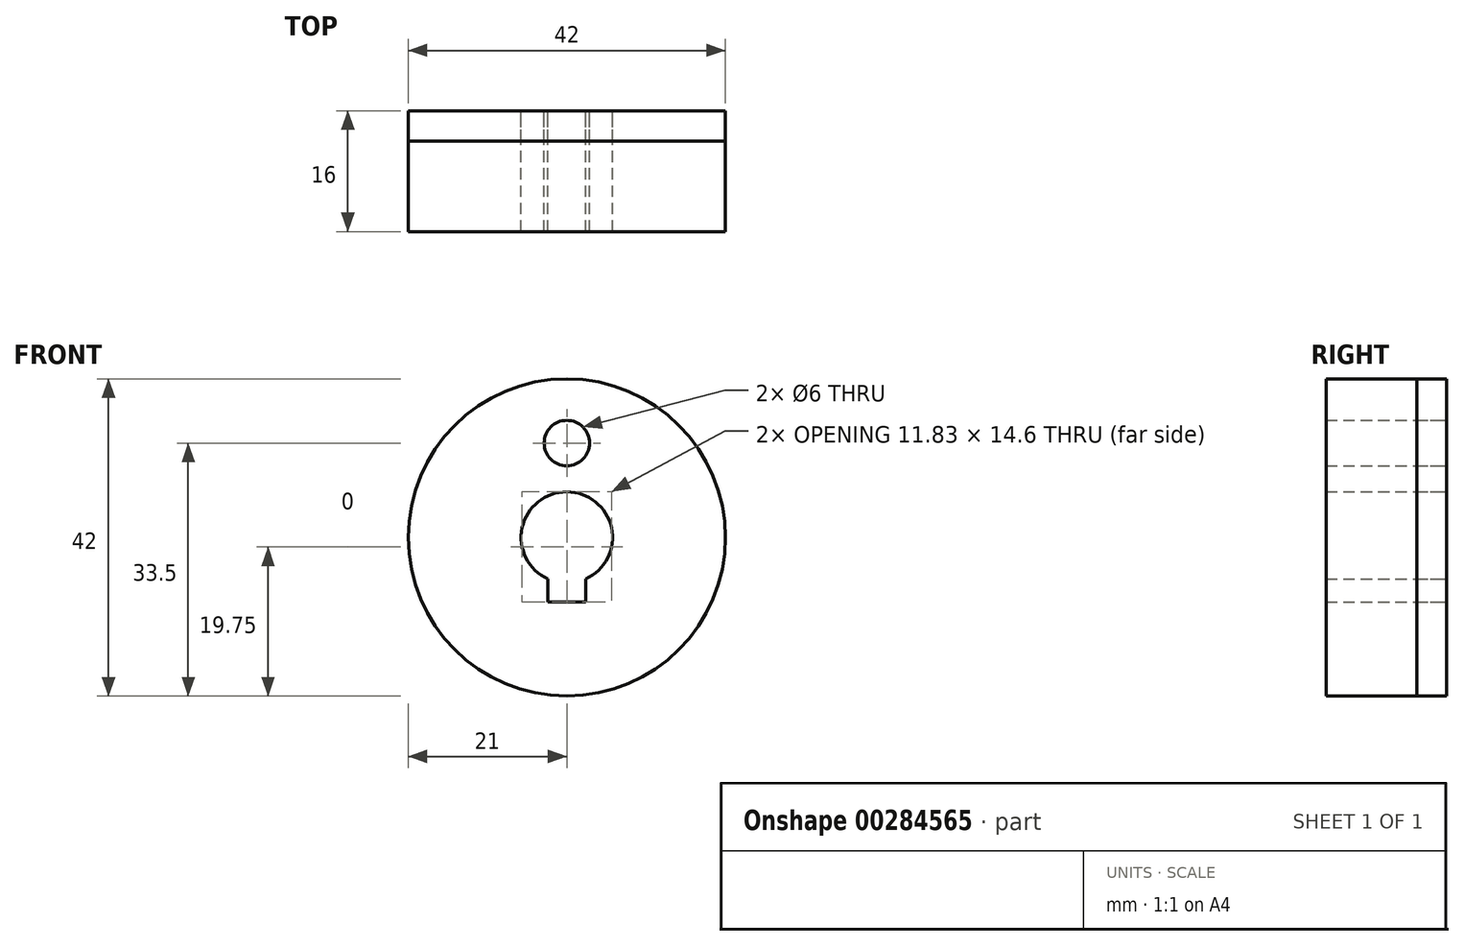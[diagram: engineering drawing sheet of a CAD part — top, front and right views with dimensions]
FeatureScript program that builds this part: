
annotation { "Feature Type Name" : "Feature", "Feature Type Description" : "" }
export const myFeature = defineFeature(function(context is Context, id is Id, definition is map)
    precondition{}
    {
        {
            var Q0;
            Q0=qCreatedBy(makeId("Front.planeOp"),FACE);
            var sketch = newSketch(context, id + "F0", { "sketchPlane" : qUnion([Q0])});
            skCircle(sketch, "E0", {"center": v(0, 0) * mm, "radius": 21 * mm});
            skArc(sketch, "E1", {"start": v(2.5, -5.5) * mm, "mid": v(0, 6.05) * mm, "end": v(-2.5, -5.5) * mm});
            skPoint(sketch, "E2", {"position": v(0, 12.5) * mm});
            skCircle(sketch, "E3", {"center": v(0, 12.5) * mm, "radius": 3 * mm});
            skLineSegment(sketch, "E4.bottom", {"start": v(-2.5, -5.5) * mm, "end": v(2.5, -5.5) * mm, "construction": true});
            skLineSegment(sketch, "E4.top", {"start": v(-2.5, -8.55) * mm, "end": v(2.5, -8.55) * mm});
            skLineSegment(sketch, "E4.left", {"start": v(-2.5, -5.5) * mm, "end": v(-2.5, -8.55) * mm});
            skLineSegment(sketch, "E4.right", {"start": v(2.5, -5.5) * mm, "end": v(2.5, -8.55) * mm});
            skSolve(sketch);
        }
        {
            var Q0;
            Q0=makeQuery(id+"F0.imprint","IMPRINT",FACE,{"disambiguationData":[TD([[makeQuery(id+"F0.imprint","IMPRINT",EDGE,{"derivedFrom":sQuery(id+"F0.wireOp",EDGE,"E0")}),1.0]])]});
            extrude(context, id + "F1", {"entities" : qUnion([Q0]), "depth" : 16 * mm});
        }
        {
            var Q0;
            Q0=qSketchRegion(id+"F0",true);
            extrude(context, id + "F2", {"entities" : qUnion([Q0]), "depth" : 4 * mm});
        }
    });
